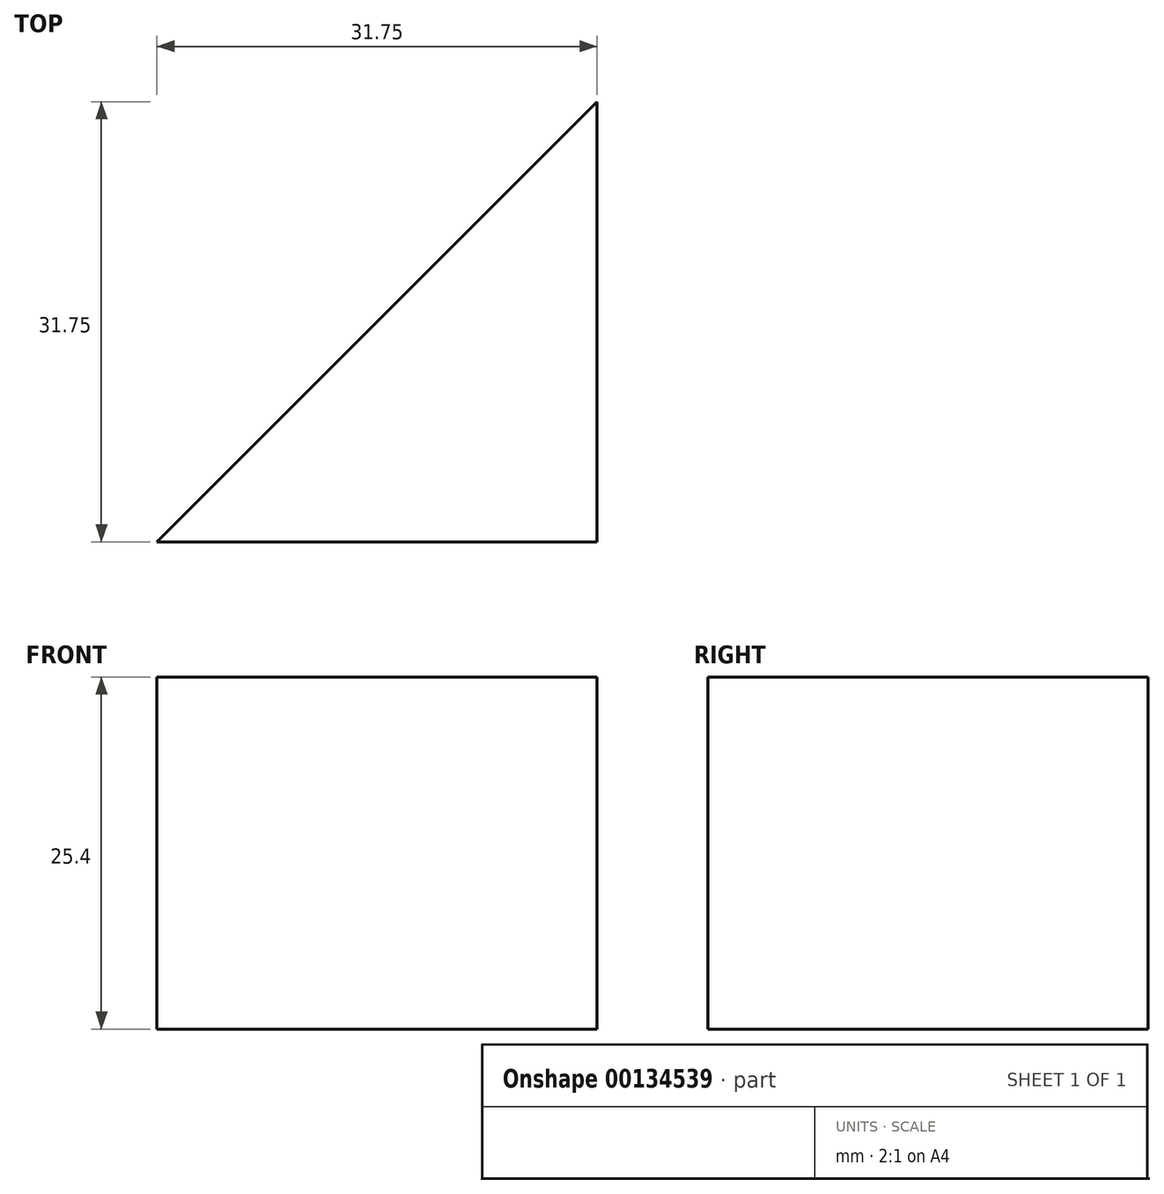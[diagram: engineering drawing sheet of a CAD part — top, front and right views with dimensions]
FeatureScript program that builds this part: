
annotation { "Feature Type Name" : "Feature", "Feature Type Description" : "" }
export const myFeature = defineFeature(function(context is Context, id is Id, definition is map)
    precondition{}
    {
        {
            var Q0;
            Q0=qCreatedBy(makeId("Top.planeOp"),FACE);
            var sketch = newSketch(context, id + "F0", { "sketchPlane" : qUnion([Q0])});
            skLineSegment(sketch, "E0", {"start": v(3.12, 3.54) * mm, "end": v(3.12, -28.21) * mm});
            skLineSegment(sketch, "E1", {"start": v(3.12, -28.21) * mm, "end": v(-28.63, -28.21) * mm});
            skLineSegment(sketch, "E2", {"start": v(-28.63, -28.21) * mm, "end": v(3.12, 3.54) * mm});
            skSolve(sketch);
        }
        {
            var Q0;
            Q0=makeQuery(id+"F0.imprint","IMPRINT",FACE,{"disambiguationData":[TD([[makeQuery(id+"F0.imprint","IMPRINT",EDGE,{"derivedFrom":sQuery(id+"F0.wireOp",EDGE,"E0")}),-1.0]])]});
            extrude(context, id + "F1", {"entities" : qUnion([Q0]), "depth" : 25.4 * mm});
        }
    });
